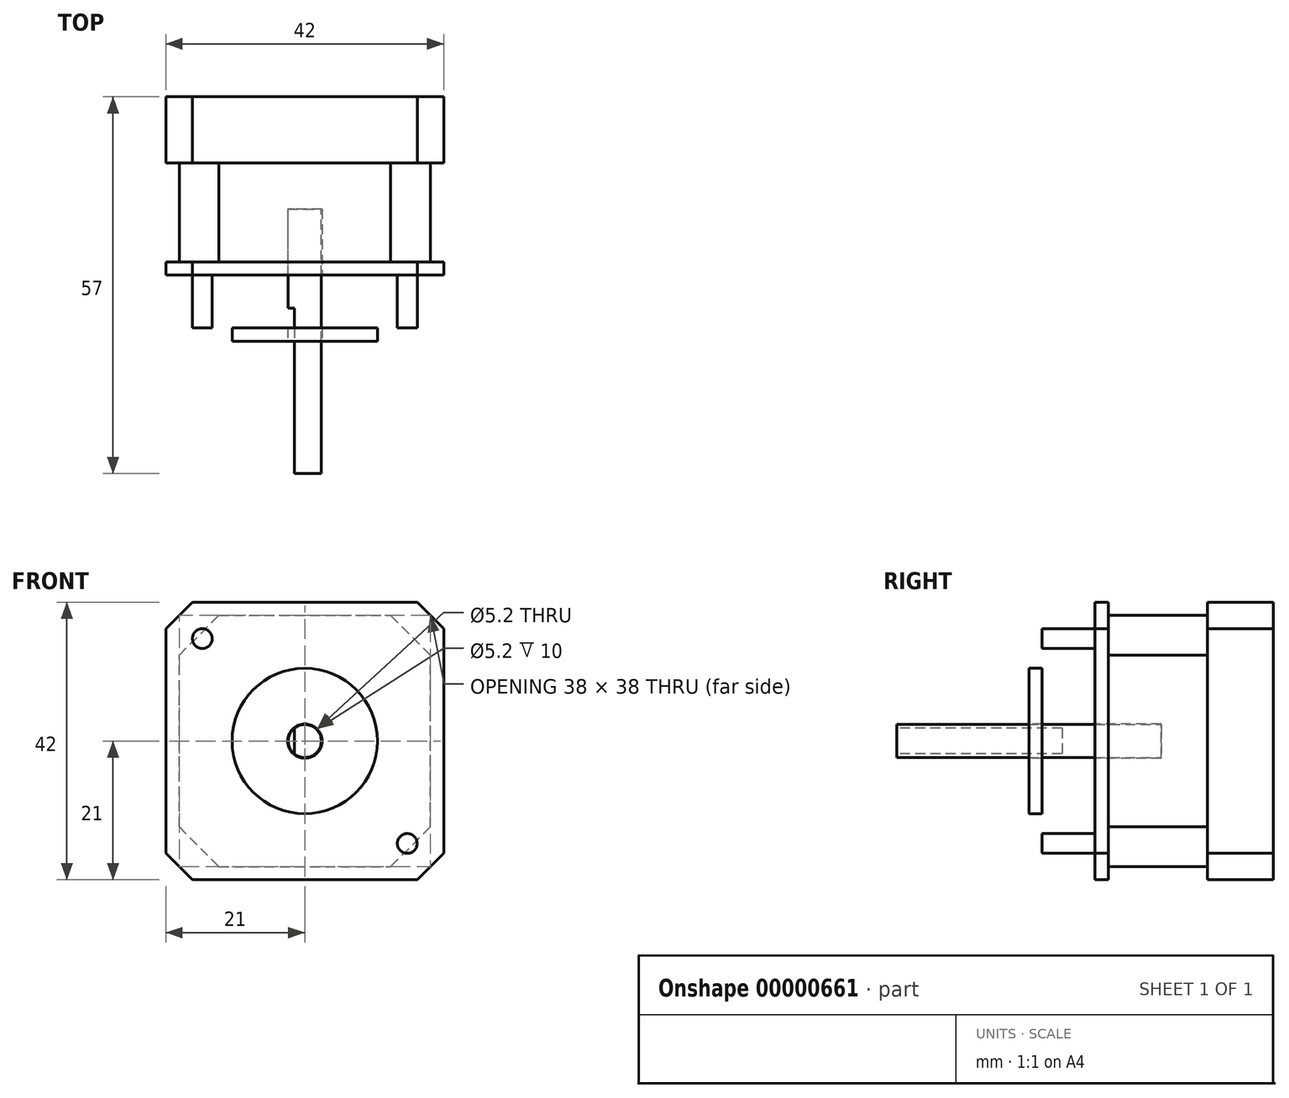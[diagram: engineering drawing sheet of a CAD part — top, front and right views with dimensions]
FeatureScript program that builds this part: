
annotation { "Feature Type Name" : "Feature", "Feature Type Description" : "" }
export const myFeature = defineFeature(function(context is Context, id is Id, definition is map)
    precondition{}
    {
        {
            var Q0;
            Q0=qCreatedBy(makeId("Front.planeOp"),FACE);
            var sketch = newSketch(context, id + "F0", { "sketchPlane" : qUnion([Q0])});
            skLineSegment(sketch, "E0.rect.bottom", {"start": v(21, 21) * mm, "end": v(-21, 21) * mm});
            skLineSegment(sketch, "E0.rect.top", {"start": v(21, -21) * mm, "end": v(-21, -21) * mm});
            skLineSegment(sketch, "E0.rect.left", {"start": v(21, 21) * mm, "end": v(21, -21) * mm});
            skLineSegment(sketch, "E0.rect.right", {"start": v(-21, 21) * mm, "end": v(-21, -21) * mm});
            skPoint(sketch, "E0.rect.middle", {"position": v(0, 0) * mm});
            skSolve(sketch);
        }
        {
            var Q0;
            Q0=makeQuery(id+"F0.imprint","IMPRINT",FACE,{"disambiguationData":[TD([[makeQuery(id+"F0.imprint","IMPRINT",EDGE,{"derivedFrom":sQuery(id+"F0.wireOp",EDGE,"E0.rect.bottom")}),1.0]])]});
            extrude(context, id + "F1", {"entities" : qUnion([Q0]), "oppositeDirection" : true, "depth" : 10 * mm});
        }
        {
            var Q0;
            Q0=makeQuery(id+"F1.opExtrude","CAP_FACE",FACE,{"disambiguationData":[OSD([sQuery(id+"F0.wireOp",EDGE,"E0.rect.bottom"),sQuery(id+"F0.wireOp",EDGE,"E0.rect.top"),sQuery(id+"F0.wireOp",EDGE,"E0.rect.left"),sQuery(id+"F0.wireOp",EDGE,"E0.rect.right")])],"isStart":false});
            var sketch = newSketch(context, id + "F2", { "sketchPlane" : qUnion([Q0])});
            skLineSegment(sketch, "E1.rect.bottom", {"start": v(19, -19) * mm, "end": v(-19, -19) * mm});
            skLineSegment(sketch, "E1.rect.top", {"start": v(19, 19) * mm, "end": v(-19, 19) * mm});
            skLineSegment(sketch, "E1.rect.left", {"start": v(19, -19) * mm, "end": v(19, 19) * mm});
            skLineSegment(sketch, "E1.rect.right", {"start": v(-19, -19) * mm, "end": v(-19, 19) * mm});
            skPoint(sketch, "E1.rect.middle", {"position": v(0, 0) * mm});
            skSolve(sketch);
        }
        {
            var Q0;
            Q0=makeQuery(id+"F2.imprint","IMPRINT",FACE,{"disambiguationData":[TD([[makeQuery(id+"F2.imprint","IMPRINT",EDGE,{"derivedFrom":sQuery(id+"F2.wireOp",EDGE,"E1.rect.bottom")}),-1.0]])]});
            extrude(context, id + "F3", {"entities" : qUnion([Q0]), "operationType" : NewBodyOperationType.ADD, "depth" : 15 * mm});
        }
        {
            var Q0;
            Q0=makeQuery(id+"F3.opExtrude","CAP_FACE",FACE,{"disambiguationData":[OSD([sQuery(id+"F2.wireOp",EDGE,"E1.rect.bottom"),sQuery(id+"F2.wireOp",EDGE,"E1.rect.top"),sQuery(id+"F2.wireOp",EDGE,"E1.rect.left"),sQuery(id+"F2.wireOp",EDGE,"E1.rect.right")])],"isStart":false});
            var sketch = newSketch(context, id + "F4", { "sketchPlane" : qUnion([Q0])});
            skLineSegment(sketch, "E2.rect.bottom", {"start": v(21, -21) * mm, "end": v(-21, -21) * mm});
            skLineSegment(sketch, "E2.rect.top", {"start": v(21, 21) * mm, "end": v(-21, 21) * mm});
            skLineSegment(sketch, "E2.rect.left", {"start": v(21, -21) * mm, "end": v(21, 21) * mm});
            skLineSegment(sketch, "E2.rect.right", {"start": v(-21, -21) * mm, "end": v(-21, 21) * mm});
            skPoint(sketch, "E2.rect.middle", {"position": v(0, 0) * mm});
            skSolve(sketch);
        }
        {
            var Q0;
            Q0=makeQuery(id+"F4.imprint","IMPRINT",FACE,{"disambiguationData":[TD([[makeQuery(id+"F4.imprint","IMPRINT",EDGE,{"derivedFrom":makeQuery(id+"F3.opExtrude","CAP_EDGE",EDGE,{"disambiguationData":[OSD([sQuery(id+"F2.wireOp",EDGE,"E1.rect.bottom")])],"isStart":false})}),-1.0]])]});
            var Q1;
            Q1=makeQuery(id+"F4.imprint","IMPRINT",FACE,{"disambiguationData":[TD([[makeQuery(id+"F4.imprint","IMPRINT",EDGE,{"derivedFrom":sQuery(id+"F4.wireOp",EDGE,"E2.rect.bottom")}),-1.0]])]});
            extrude(context, id + "F5", {"entities" : qUnion([Q0, Q1]), "operationType" : NewBodyOperationType.ADD, "depth" : 10 * mm});
        }
        {
            var Q0;
            Q0=makeQuery(id+"F3.opExtrude","SWEPT_EDGE",EDGE,{"disambiguationData":[OSD([sQuery(id+"F2.wireOp",EDGE,"E1.rect.bottom"),sQuery(id+"F2.wireOp",EDGE,"E1.rect.right")])]});
            var Q1;
            Q1=makeQuery(id+"F3.opExtrude","SWEPT_EDGE",EDGE,{"disambiguationData":[OSD([sQuery(id+"F2.wireOp",EDGE,"E1.rect.top"),sQuery(id+"F2.wireOp",EDGE,"E1.rect.right")])]});
            var Q2;
            Q2=makeQuery(id+"F3.opExtrude","SWEPT_EDGE",EDGE,{"disambiguationData":[OSD([sQuery(id+"F2.wireOp",EDGE,"E1.rect.top"),sQuery(id+"F2.wireOp",EDGE,"E1.rect.left")])]});
            var Q3;
            Q3=makeQuery(id+"F3.opExtrude","SWEPT_EDGE",EDGE,{"disambiguationData":[OSD([sQuery(id+"F2.wireOp",EDGE,"E1.rect.bottom"),sQuery(id+"F2.wireOp",EDGE,"E1.rect.left")])]});
            chamfer(context, id + "F6", {"entities" : qUnion([Q0, Q1, Q2, Q3]), "width" : 6 * mm, "tangentPropagation" : true});
        }
        {
            var Q0;
            Q0=makeQuery(id+"F1.opExtrude","SWEPT_EDGE",EDGE,{"disambiguationData":[OSD([sQuery(id+"F0.wireOp",EDGE,"E0.rect.top"),sQuery(id+"F0.wireOp",EDGE,"E0.rect.right")])]});
            var Q1;
            Q1=makeQuery(id+"F1.opExtrude","SWEPT_EDGE",EDGE,{"disambiguationData":[OSD([sQuery(id+"F0.wireOp",EDGE,"E0.rect.bottom"),sQuery(id+"F0.wireOp",EDGE,"E0.rect.right")])]});
            var Q2;
            Q2=makeQuery(id+"F1.opExtrude","SWEPT_EDGE",EDGE,{"disambiguationData":[OSD([sQuery(id+"F0.wireOp",EDGE,"E0.rect.top"),sQuery(id+"F0.wireOp",EDGE,"E0.rect.left")])]});
            var Q3;
            Q3=makeQuery(id+"F1.opExtrude","SWEPT_EDGE",EDGE,{"disambiguationData":[OSD([sQuery(id+"F0.wireOp",EDGE,"E0.rect.bottom"),sQuery(id+"F0.wireOp",EDGE,"E0.rect.left")])]});
            var Q4;
            Q4=makeQuery(id+"F5.opExtrude","SWEPT_EDGE",EDGE,{"disambiguationData":[OSD([sQuery(id+"F4.wireOp",EDGE,"E2.rect.bottom"),sQuery(id+"F4.wireOp",EDGE,"E2.rect.right")])]});
            var Q5;
            Q5=makeQuery(id+"F5.opExtrude","SWEPT_EDGE",EDGE,{"disambiguationData":[OSD([sQuery(id+"F4.wireOp",EDGE,"E2.rect.top"),sQuery(id+"F4.wireOp",EDGE,"E2.rect.right")])]});
            var Q6;
            Q6=makeQuery(id+"F5.opExtrude","SWEPT_EDGE",EDGE,{"disambiguationData":[OSD([sQuery(id+"F4.wireOp",EDGE,"E2.rect.bottom"),sQuery(id+"F4.wireOp",EDGE,"E2.rect.left")])]});
            var Q7;
            Q7=makeQuery(id+"F5.opExtrude","SWEPT_EDGE",EDGE,{"disambiguationData":[OSD([sQuery(id+"F4.wireOp",EDGE,"E2.rect.top"),sQuery(id+"F4.wireOp",EDGE,"E2.rect.left")])]});
            chamfer(context, id + "F7", {"entities" : qUnion([Q0, Q1, Q2, Q3, Q4, Q5, Q6, Q7]), "width" : 4 * mm, "tangentPropagation" : true});
        }
        {
            var Q0;
            Q0=makeQuery(id+"F1.opExtrude","CAP_FACE",FACE,{"disambiguationData":[OSD([sQuery(id+"F0.wireOp",EDGE,"E0.rect.bottom"),sQuery(id+"F0.wireOp",EDGE,"E0.rect.top"),sQuery(id+"F0.wireOp",EDGE,"E0.rect.left"),sQuery(id+"F0.wireOp",EDGE,"E0.rect.right")])],"isStart":true});
            var sketch = newSketch(context, id + "F8", { "sketchPlane" : qUnion([Q0])});
            skCircle(sketch, "E3", {"center": v(-15.5, -15.5) * mm, "radius": 1.5 * mm});
            skLineSegment(sketch, "E4", {"start": v(0, -40.98) * mm, "end": v(0, 34.94) * mm, "construction": true});
            skCircle(sketch, "E5.0.MirrorC", {"center": v(15.5, -15.5) * mm, "radius": 1.5 * mm});
            skLineSegment(sketch, "E6", {"start": v(0, 0) * mm, "end": v(49.43, 0) * mm, "construction": true});
            skCircle(sketch, "E7.0.MirrorC", {"center": v(15.5, 15.5) * mm, "radius": 1.5 * mm});
            skCircle(sketch, "E8.0.MirrorC", {"center": v(-15.5, 15.5) * mm, "radius": 1.5 * mm});
            skSolve(sketch);
        }
        {
            var Q0;
            {Q0=qUnion([makeQuery(id+"F8.imprint","IMPRINT",FACE,{"disambiguationData":[TD([[makeQuery(id+"F8.imprint","IMPRINT",EDGE,{"derivedFrom":sQuery(id+"F8.wireOp",EDGE,"E3")}),1.0]])]}),makeQuery(id+"F8.imprint","IMPRINT",FACE,{"disambiguationData":[TD([[makeQuery(id+"F8.imprint","IMPRINT",EDGE,{"derivedFrom":sQuery(id+"F8.wireOp",EDGE,"E5.0.MirrorC")}),-1.0]])]}),makeQuery(id+"F8.imprint","IMPRINT",FACE,{"disambiguationData":[TD([[makeQuery(id+"F8.imprint","IMPRINT",EDGE,{"derivedFrom":sQuery(id+"F8.wireOp",EDGE,"E7.0.MirrorC")}),1.0]])]}),makeQuery(id+"F8.imprint","IMPRINT",FACE,{"disambiguationData":[TD([[makeQuery(id+"F8.imprint","IMPRINT",EDGE,{"derivedFrom":sQuery(id+"F8.wireOp",EDGE,"E8.0.MirrorC")}),-1.0]])]})]);}
            extrude(context, id + "F9", {"entities" : qUnion([Q0]), "operationType" : NewBodyOperationType.REMOVE, "oppositeDirection" : true, "depth" : 8 * mm});
        }
        {
            var Q0;
            Q0=makeQuery(id+"F1.opExtrude","CAP_FACE",FACE,{"disambiguationData":[OSD([sQuery(id+"F0.wireOp",EDGE,"E0.rect.bottom"),sQuery(id+"F0.wireOp",EDGE,"E0.rect.top"),sQuery(id+"F0.wireOp",EDGE,"E0.rect.left"),sQuery(id+"F0.wireOp",EDGE,"E0.rect.right")])],"isStart":true});
            var sketch = newSketch(context, id + "F10", { "sketchPlane" : qUnion([Q0])});
            skCircle(sketch, "E9", {"center": v(0, 0) * mm, "radius": 11 * mm});
            skSolve(sketch);
        }
        {
            var Q0;
            Q0=makeQuery(id+"F10.imprint","IMPRINT",FACE,{"disambiguationData":[TD([[makeQuery(id+"F10.imprint","IMPRINT",EDGE,{"derivedFrom":sQuery(id+"F10.wireOp",EDGE,"E9")}),1.0]])]});
            extrude(context, id + "F11", {"entities" : qUnion([Q0]), "operationType" : NewBodyOperationType.ADD, "depth" : 2 * mm});
        }
        {
            var Q0;
            Q0=makeQuery(id+"F11.opExtrude","CAP_FACE",FACE,{"disambiguationData":[OSD([sQuery(id+"F10.wireOp",EDGE,"E9")])],"isStart":false});
            var sketch = newSketch(context, id + "F12", { "sketchPlane" : qUnion([Q0])});
            skCircle(sketch, "E10", {"center": v(0, 0) * mm, "radius": 2.6 * mm});
            skSolve(sketch);
        }
        {
            var Q0;
            Q0=makeQuery(id+"F12.imprint","IMPRINT",FACE,{"disambiguationData":[TD([[makeQuery(id+"F12.imprint","IMPRINT",EDGE,{"derivedFrom":sQuery(id+"F12.wireOp",EDGE,"E10")}),1.0]])]});
            extrude(context, id + "F13", {"entities" : qUnion([Q0]), "operationType" : NewBodyOperationType.REMOVE, "oppositeDirection" : true, "depth" : 20 * mm});
        }
        {
            var Q0;
            Q0=makeQuery(id+"F11.opExtrude","CAP_FACE",FACE,{"disambiguationData":[OSD([sQuery(id+"F10.wireOp",EDGE,"E9")])],"isStart":false});
            var sketch = newSketch(context, id + "F14", { "sketchPlane" : qUnion([Q0])});
            skCircle(sketch, "E11", {"center": v(0, 0) * mm, "radius": 2.5 * mm});
            skSolve(sketch);
        }
        {
            var Q0;
            Q0=makeQuery(id+"F14.imprint","IMPRINT",FACE,{"disambiguationData":[TD([[makeQuery(id+"F14.imprint","IMPRINT",EDGE,{"derivedFrom":sQuery(id+"F14.wireOp",EDGE,"E11")}),1.0]])]});
            extrude(context, id + "F15", {"entities" : qUnion([Q0]), "depth" : 40 * mm, "symmetric" : true});
        }
        {
            var Q0;
            Q0=makeQuery(id+"F15.opExtrude","CAP_FACE",FACE,{"disambiguationData":[OSD([sQuery(id+"F14.wireOp",EDGE,"E11")])],"isStart":false});
            var sketch = newSketch(context, id + "F16", { "sketchPlane" : qUnion([Q0])});
            skArc(sketch, "E12", {"start": v(-1.56, 1.95) * mm, "mid": v(-2.5, 0) * mm, "end": v(-1.56, -1.95) * mm});
            skLineSegment(sketch, "E13", {"start": v(-1.56, 1.95) * mm, "end": v(-1.56, -1.95) * mm});
            skSolve(sketch);
        }
        {
            var Q0;
            Q0=makeQuery(id+"F16.imprint","IMPRINT",FACE,{"disambiguationData":[TD([[makeQuery(id+"F16.imprint","IMPRINT",EDGE,{"derivedFrom":sQuery(id+"F16.wireOp",EDGE,"E12")}),1.0]])]});
            extrude(context, id + "F17", {"entities" : qUnion([Q0]), "operationType" : NewBodyOperationType.REMOVE, "oppositeDirection" : true, "depth" : 25 * mm});
        }
    });
